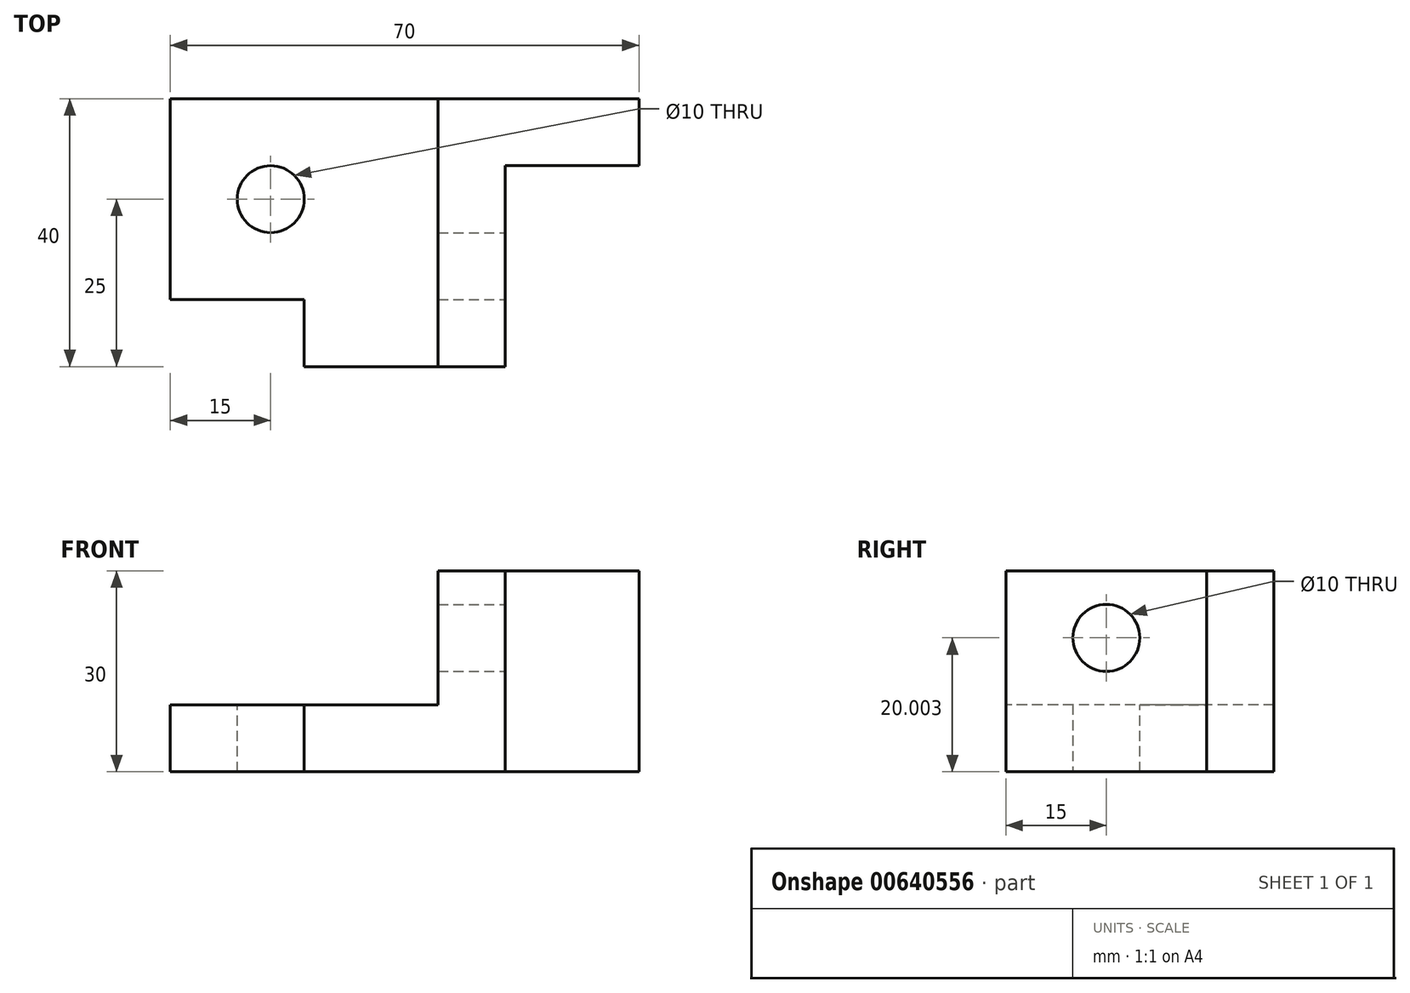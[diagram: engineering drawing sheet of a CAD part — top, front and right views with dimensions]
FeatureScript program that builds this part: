
annotation { "Feature Type Name" : "Feature", "Feature Type Description" : "" }
export const myFeature = defineFeature(function(context is Context, id is Id, definition is map)
    precondition{}
    {
        {
            var Q0;
            Q0=qCreatedBy(makeId("Front.planeOp"),FACE);
            var sketch = newSketch(context, id + "F0", { "sketchPlane" : qUnion([Q0])});
            skLineSegment(sketch, "E0", {"start": v(-5.38, 4.75) * mm, "end": v(24.62, 4.75) * mm});
            skLineSegment(sketch, "E1", {"start": v(24.62, 4.75) * mm, "end": v(24.62, 34.75) * mm});
            skLineSegment(sketch, "E2", {"start": v(24.62, 34.75) * mm, "end": v(14.62, 34.75) * mm});
            skLineSegment(sketch, "E3", {"start": v(14.62, 34.75) * mm, "end": v(14.62, 14.75) * mm});
            skLineSegment(sketch, "E4", {"start": v(14.62, 14.75) * mm, "end": v(-5.38, 14.75) * mm});
            skLineSegment(sketch, "E5", {"start": v(-5.38, 4.75) * mm, "end": v(-5.38, 14.75) * mm});
            skSolve(sketch);
        }
        {
            var Q0;
            Q0 = qSketchRegion(id + "F0", true);
            extrude(context, id + "F1", {"entities" : qUnion([Q0]), "oppositeDirection" : true, "depth" : 40 * mm, "offsetDistance" : 25 * mm});
        }
        {
            var Q0;
            Q0=makeQuery(id+"F1.opExtrude","SWEPT_FACE",FACE,{"disambiguationData":[OSD([sQuery(id+"F0.wireOp",EDGE,"E1")])]});
            var sketch = newSketch(context, id + "F2", { "sketchPlane" : qUnion([Q0])});
            skLineSegment(sketch, "E6.bottom", {"start": v(30, 34.75) * mm, "end": v(40, 34.75) * mm});
            skLineSegment(sketch, "E6.top", {"start": v(30, 4.75) * mm, "end": v(40, 4.75) * mm});
            skLineSegment(sketch, "E6.left", {"start": v(30, 34.75) * mm, "end": v(30, 4.75) * mm});
            skLineSegment(sketch, "E6.right", {"start": v(40, 34.75) * mm, "end": v(40, 4.75) * mm});
            skSolve(sketch);
        }
        {
            var Q0;
            Q0=makeQuery(id+"F2.imprint","IMPRINT",FACE,{"disambiguationData":[TD([[makeQuery(id+"F2.imprint","IMPRINT",EDGE,{"derivedFrom":sQuery(id+"F2.wireOp",EDGE,"E6.bottom")}),1.0]])]});
            extrude(context, id + "F3", {"entities" : qUnion([Q0]), "operationType" : NewBodyOperationType.ADD, "depth" : 20 * mm, "offsetDistance" : 25 * mm});
        }
        {
            var Q0;
            Q0=makeQuery(id+"F1.opExtrude","SWEPT_FACE",FACE,{"disambiguationData":[OSD([sQuery(id+"F0.wireOp",EDGE,"E1")])]});
            var sketch = newSketch(context, id + "F4", { "sketchPlane" : qUnion([Q0])});
            skLineSegment(sketch, "E7", {"start": v(15, 34.75) * mm, "end": v(15, 24.75) * mm, "construction": true});
            skCircle(sketch, "E8", {"center": v(15, 24.75) * mm, "radius": 5 * mm});
            skSolve(sketch);
        }
        {
            var Q0;
            Q0=makeQuery(id+"F4.imprint","IMPRINT",FACE,{"disambiguationData":[TD([[makeQuery(id+"F4.imprint","IMPRINT",EDGE,{"derivedFrom":sQuery(id+"F4.wireOp",EDGE,"E8")}),1.0]])]});
            var Q1;
            Q1=sQuery(id+"F4.wireOp",EDGE,"E8");
            extrude(context, id + "F5", {"entities" : qUnion([Q0]), "operationType" : NewBodyOperationType.REMOVE, "surfaceEntities" : qUnion([Q1]), "endBound" : BoundingType.THROUGH_ALL, "oppositeDirection" : true, "depth" : 25 * mm, "offsetDistance" : 25 * mm});
        }
        {
            var Q0;
            Q0=makeQuery(id+"F1.opExtrude","SWEPT_FACE",FACE,{"disambiguationData":[OSD([sQuery(id+"F0.wireOp",EDGE,"E5")])]});
            var sketch = newSketch(context, id + "F6", { "sketchPlane" : qUnion([Q0])});
            skLineSegment(sketch, "E9.bottom", {"start": v(-40, 14.75) * mm, "end": v(-10, 14.75) * mm});
            skLineSegment(sketch, "E9.top", {"start": v(-40, 4.75) * mm, "end": v(-10, 4.75) * mm});
            skLineSegment(sketch, "E9.left", {"start": v(-40, 14.75) * mm, "end": v(-40, 4.75) * mm});
            skLineSegment(sketch, "E9.right", {"start": v(-10, 14.75) * mm, "end": v(-10, 4.75) * mm});
            skSolve(sketch);
        }
        {
            var Q0;
            Q0=makeQuery(id+"F6.imprint","IMPRINT",FACE,{"disambiguationData":[TD([[makeQuery(id+"F6.imprint","IMPRINT",EDGE,{"derivedFrom":sQuery(id+"F6.wireOp",EDGE,"E9.bottom")}),-1.0]])]});
            extrude(context, id + "F7", {"entities" : qUnion([Q0]), "operationType" : NewBodyOperationType.ADD, "depth" : 20 * mm, "offsetDistance" : 25 * mm});
        }
        {
            var Q0;
            Q0=makeQuery(id+"F7.boolean.opBoolean","MERGE",FACE,{"derivedFrom":[makeQuery(id+"F1.opExtrude","SWEPT_FACE",FACE,{"disambiguationData":[OSD([sQuery(id+"F0.wireOp",EDGE,"E4")])]}),makeQuery(id+"F7.opExtrude","SWEPT_FACE",FACE,{"disambiguationData":[OSD([sQuery(id+"F6.wireOp",EDGE,"E9.bottom")])]})]});
            var sketch = newSketch(context, id + "F8", { "sketchPlane" : qUnion([Q0])});
            skLineSegment(sketch, "E10", {"start": v(-25.38, 25) * mm, "end": v(-10.38, 25) * mm, "construction": true});
            skCircle(sketch, "E11", {"center": v(-10.38, 25) * mm, "radius": 5 * mm});
            skSolve(sketch);
        }
        {
            var Q0;
            Q0=makeQuery(id+"F8.imprint","IMPRINT",FACE,{"disambiguationData":[TD([[makeQuery(id+"F8.imprint","IMPRINT",EDGE,{"derivedFrom":sQuery(id+"F8.wireOp",EDGE,"E11")}),1.0]])]});
            extrude(context, id + "F9", {"entities" : qUnion([Q0]), "operationType" : NewBodyOperationType.REMOVE, "endBound" : BoundingType.THROUGH_ALL, "oppositeDirection" : true, "depth" : 25 * mm, "offsetDistance" : 25 * mm});
        }
    });
